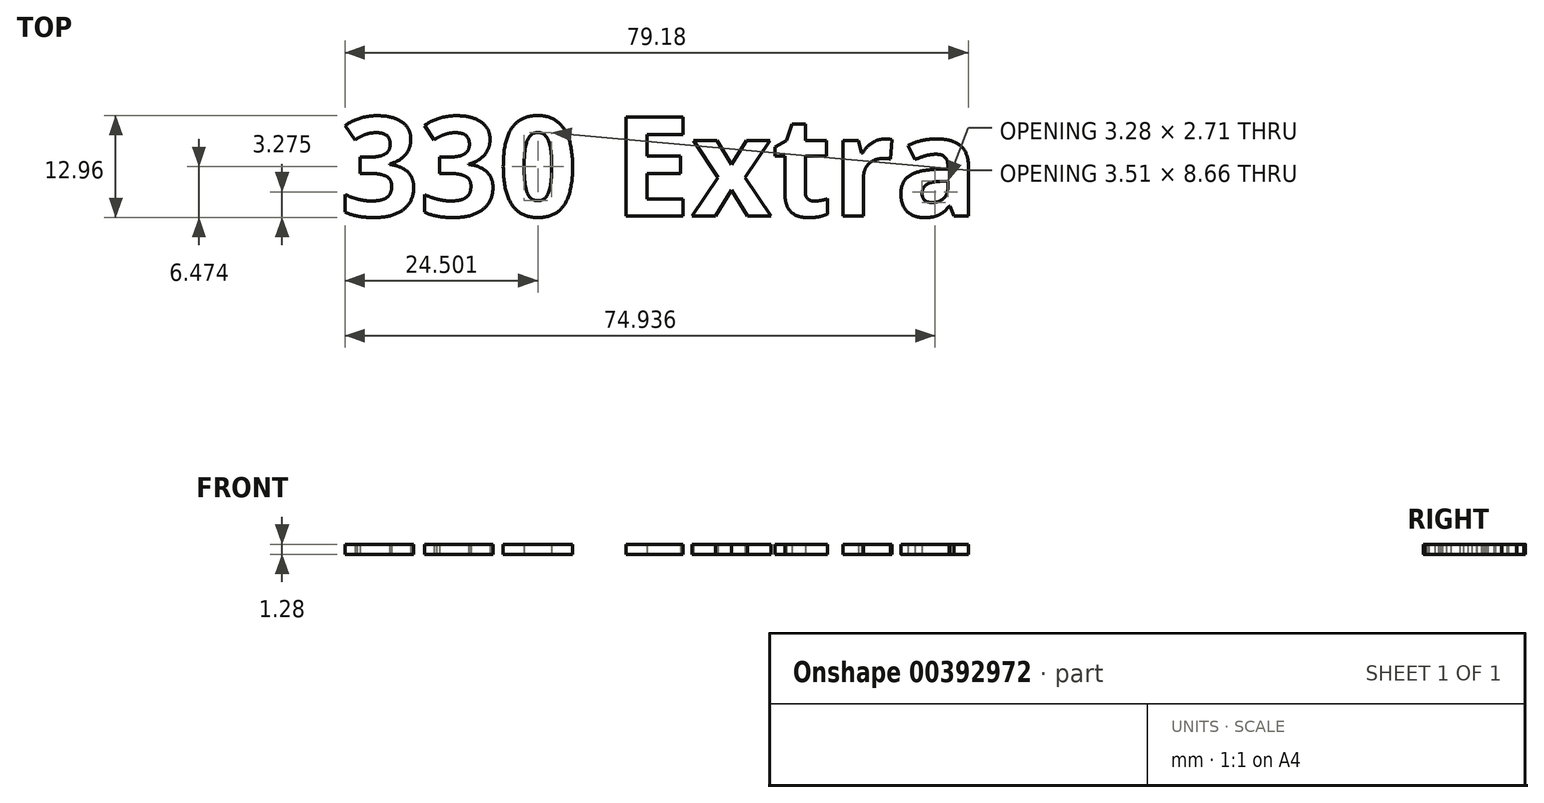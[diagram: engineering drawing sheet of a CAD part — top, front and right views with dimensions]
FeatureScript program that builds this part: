
annotation { "Feature Type Name" : "Feature", "Feature Type Description" : "" }
export const myFeature = defineFeature(function(context is Context, id is Id, definition is map)
    precondition{}
    {
        {
            var Q0;
            Q0=qCreatedBy(makeId("Top.planeOp"),FACE);
            var sketch = newSketch(context, id + "F0", { "sketchPlane" : qUnion([Q0])});
            skLineSegment(sketch, "E0", {"start": v(-50.8, 0) * mm, "end": v(50.8, 0) * mm});
            skFitSpline(sketch, "E1", {"points": [v(-50.8, 0) * mm, v(0, 76.2) * mm], "startDerivative": vector(18.65, 86.3) * mm, "endDerivative": vector(99.9, 11.1) * mm});
            skFitSpline(sketch, "E2.MirrorCS", {"points": [v(50.8, 0) * mm, v(0, 76.2) * mm], "startDerivative": vector(-18.65, 86.3) * mm, "endDerivative": vector(-99.9, 11.1) * mm});
            skFitSpline(sketch, "E3.0", {"points": [v(-44.6, -1.34) * mm, v(-43.82, 2.22) * mm, v(-42.14, 9.77) * mm, v(-38.97, 21.7) * mm, v(-35, 33.62) * mm, v(-30.1, 44.81) * mm, v(-25.13, 52.98) * mm, v(-20.63, 58.5) * mm, v(-17, 62.09) * mm, v(-13.1, 65.05) * mm, v(-8.9, 67.38) * mm, v(-4.37, 69.05) * mm, v(-1.05, 69.7) * mm, v(0.7, 69.89) * mm]});
            skLineSegment(sketch, "E4", {"start": v(0, 0) * mm, "end": v(0, 76.2) * mm, "construction": true});
            skLineSegment(sketch, "E5", {"start": v(-37.7, 25.4) * mm, "end": v(0, 25.4) * mm});
            skLineSegment(sketch, "E6.MirrorCS", {"start": v(0, 50.8) * mm, "end": v(0, -25.4) * mm, "construction": true});
            skFitSpline(sketch, "E7.0", {"points": [v(44.6, -1.34) * mm, v(43.82, 2.22) * mm, v(42.14, 9.77) * mm, v(38.97, 21.7) * mm, v(35, 33.62) * mm, v(30.1, 44.81) * mm, v(25.13, 52.98) * mm, v(20.63, 58.5) * mm, v(17, 62.09) * mm, v(13.1, 65.05) * mm, v(8.9, 67.38) * mm, v(4.37, 69.05) * mm, v(1.05, 69.7) * mm, v(-0.7, 69.89) * mm]});
            skLineSegment(sketch, "E8", {"start": v(0, 25.4) * mm, "end": v(37.7, 25.4) * mm});
            skSolve(sketch);
        }
        {
            var Q0;
            Q0=makeQuery(id+"F0.imprint","IMPRINT",FACE,{"disambiguationData":[TD([[makeQuery(id+"F0.imprint","IMPRINT",EDGE,{"derivedFrom":sQuery(id+"F0.wireOp",EDGE,"E0")}),1.0]])]});
            extrude(context, id + "F1", {"entities" : qUnion([Q0]), "depth" : 1.9 * mm});
        }
        {
            var Q0;
            Q0=makeQuery(id+"F1.opExtrude","CAP_FACE",FACE,{"disambiguationData":[OSD([sQuery(id+"F0.wireOp",EDGE,"E0"),sQuery(id+"F0.wireOp",EDGE,"E1"),sQuery(id+"F0.wireOp",EDGE,"E2.MirrorCS"),sQuery(id+"F0.wireOp",EDGE,"E3.0"),sQuery(id+"F0.wireOp",EDGE,"E5"),sQuery(id+"F0.wireOp",EDGE,"E7.0"),sQuery(id+"F0.wireOp",EDGE,"E8")])],"isStart":false});
            fillet(context, id + "F2", {"entities" : qUnion([Q0]), "radius" : 1.27 * mm, "tangentPropagation" : true, "allowEdgeOverflow" : false});
        }
        {
            var Q0;
            Q0=makeQuery(id+"F1.opExtrude","CAP_FACE",FACE,{"disambiguationData":[OSD([sQuery(id+"F0.wireOp",EDGE,"E0"),sQuery(id+"F0.wireOp",EDGE,"E1"),sQuery(id+"F0.wireOp",EDGE,"E2.MirrorCS"),sQuery(id+"F0.wireOp",EDGE,"E3.0"),sQuery(id+"F0.wireOp",EDGE,"E5"),sQuery(id+"F0.wireOp",EDGE,"E7.0"),sQuery(id+"F0.wireOp",EDGE,"E8")])],"isStart":false});
            var sketch = newSketch(context, id + "F3", { "sketchPlane" : qUnion([Q0])});
            skText(sketch, "E9", { "text": "330 Extra", "fontName": "OpenSans-Bold.ttf"});
            const initialGuessF3  = {"E9": [-0.0405, 0.00762, 1, 0, 0.0127]};
            skSetInitialGuess(sketch, initialGuessF3);
            skSolve(sketch);
        }
        {
            var Q0;
            Q0=qSketchRegion(id+"F3",true);
            extrude(context, id + "F4", {"entities" : qUnion([Q0]), "depth" : 1.27 * mm});
        }
        {
            var Q0;
            Q0=makeQuery(id+"F1.opExtrude","SWEPT_BODY",BODY,{"disambiguationData":[OSD([sQuery(id+"F0.wireOp",EDGE,"E0"),sQuery(id+"F0.wireOp",EDGE,"E1"),sQuery(id+"F0.wireOp",EDGE,"E2.MirrorCS"),sQuery(id+"F0.wireOp",EDGE,"E3.0"),sQuery(id+"F0.wireOp",EDGE,"E5"),sQuery(id+"F0.wireOp",EDGE,"E7.0"),sQuery(id+"F0.wireOp",EDGE,"E8")])]});
            deleteBodies(context, id + "F5", {"entities" : qUnion([Q0])});
        }
    });
